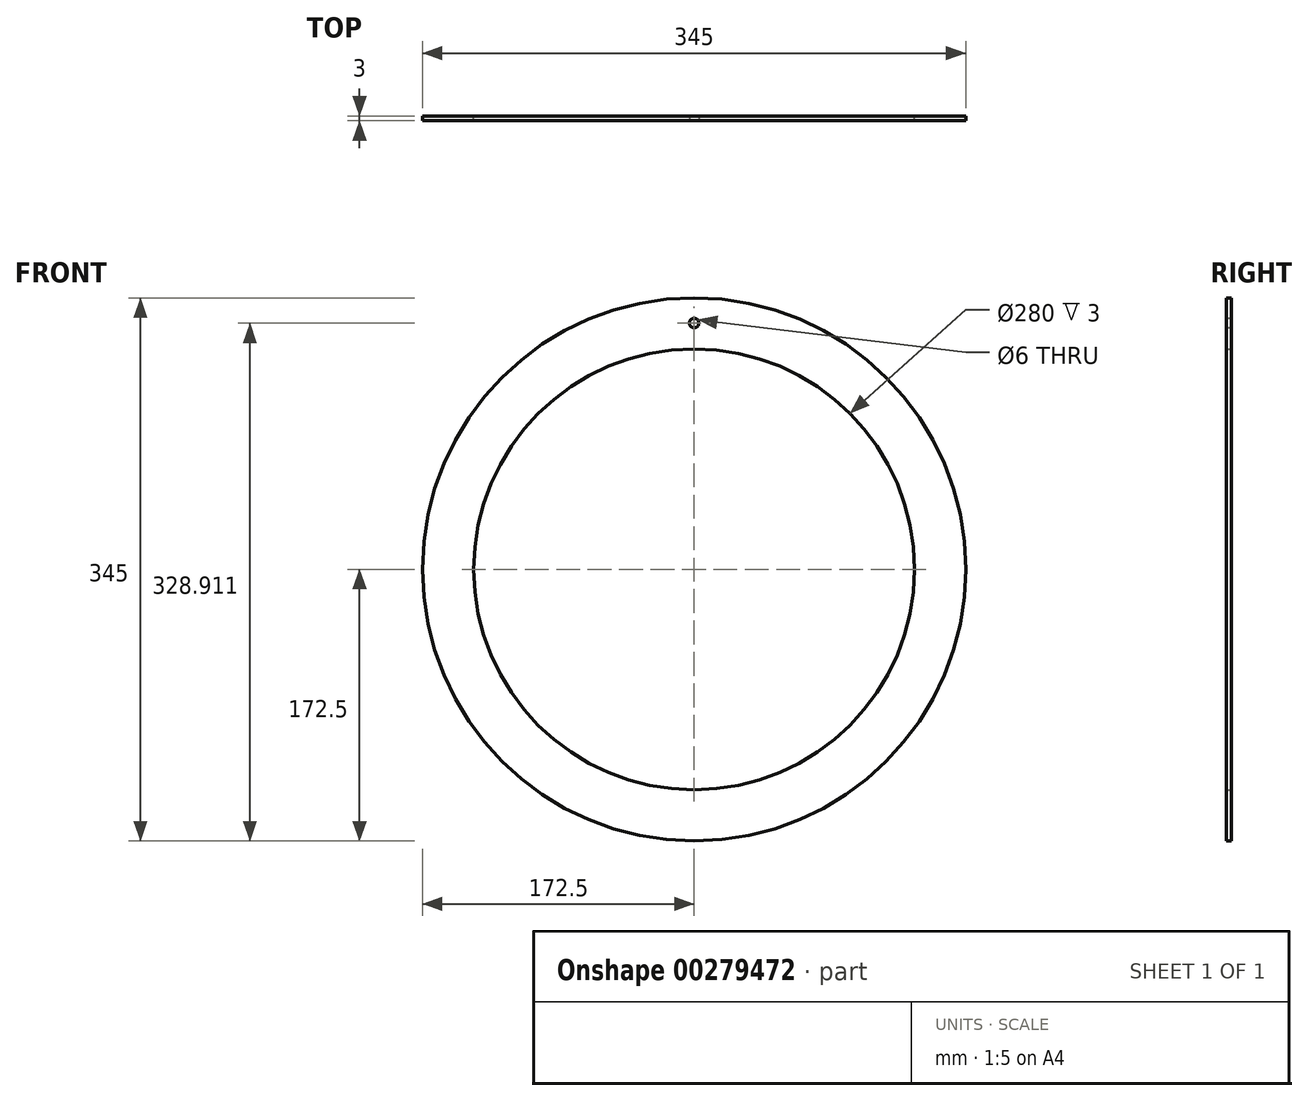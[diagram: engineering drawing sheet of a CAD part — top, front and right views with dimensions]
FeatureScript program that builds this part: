
annotation { "Feature Type Name" : "Feature", "Feature Type Description" : "" }
export const myFeature = defineFeature(function(context is Context, id is Id, definition is map)
    precondition{}
    {
        {
            var Q0;
            Q0=qCreatedBy(makeId("Front.planeOp"),FACE);
            var sketch = newSketch(context, id + "F0", { "sketchPlane" : qUnion([Q0])});
            skCircle(sketch, "E0", {"center": v(0, 0) * mm, "radius": 172.5 * mm});
            skCircle(sketch, "E1", {"center": v(0, 0) * mm, "radius": 140 * mm});
            skSolve(sketch);
        }
        {
            var Q0;
            Q0 = qSketchRegion(id + "F0", true);
            extrude(context, id + "F1", {"entities" : qUnion([Q0]), "depth" : 3 * mm});
        }
        {
            var Q0;
            Q0=makeQuery(id+"F1.opExtrude","CAP_FACE",FACE,{"disambiguationData":[OSD([sQuery(id+"F0.wireOp",EDGE,"E0"),sQuery(id+"F0.wireOp",EDGE,"E1")])],"isStart":false});
            var sketch = newSketch(context, id + "F2", { "sketchPlane" : qUnion([Q0])});
            skCircle(sketch, "E2", {"center": v(0, 156.41) * mm, "radius": 3 * mm});
            skSolve(sketch);
        }
        {
            var Q0;
            Q0=makeQuery(id+"F2.imprint","IMPRINT",FACE,{"disambiguationData":[TD([[makeQuery(id+"F2.imprint","IMPRINT",EDGE,{"derivedFrom":sQuery(id+"F2.wireOp",EDGE,"E2")}),1.0]])]});
            var Q1;
            Q1=sQuery(id+"F2.wireOp",EDGE,"E2");
            extrude(context, id + "F3", {"entities" : qUnion([Q0]), "operationType" : NewBodyOperationType.REMOVE, "surfaceEntities" : qUnion([Q1]), "oppositeDirection" : true, "depth" : 25 * mm});
        }
    });
